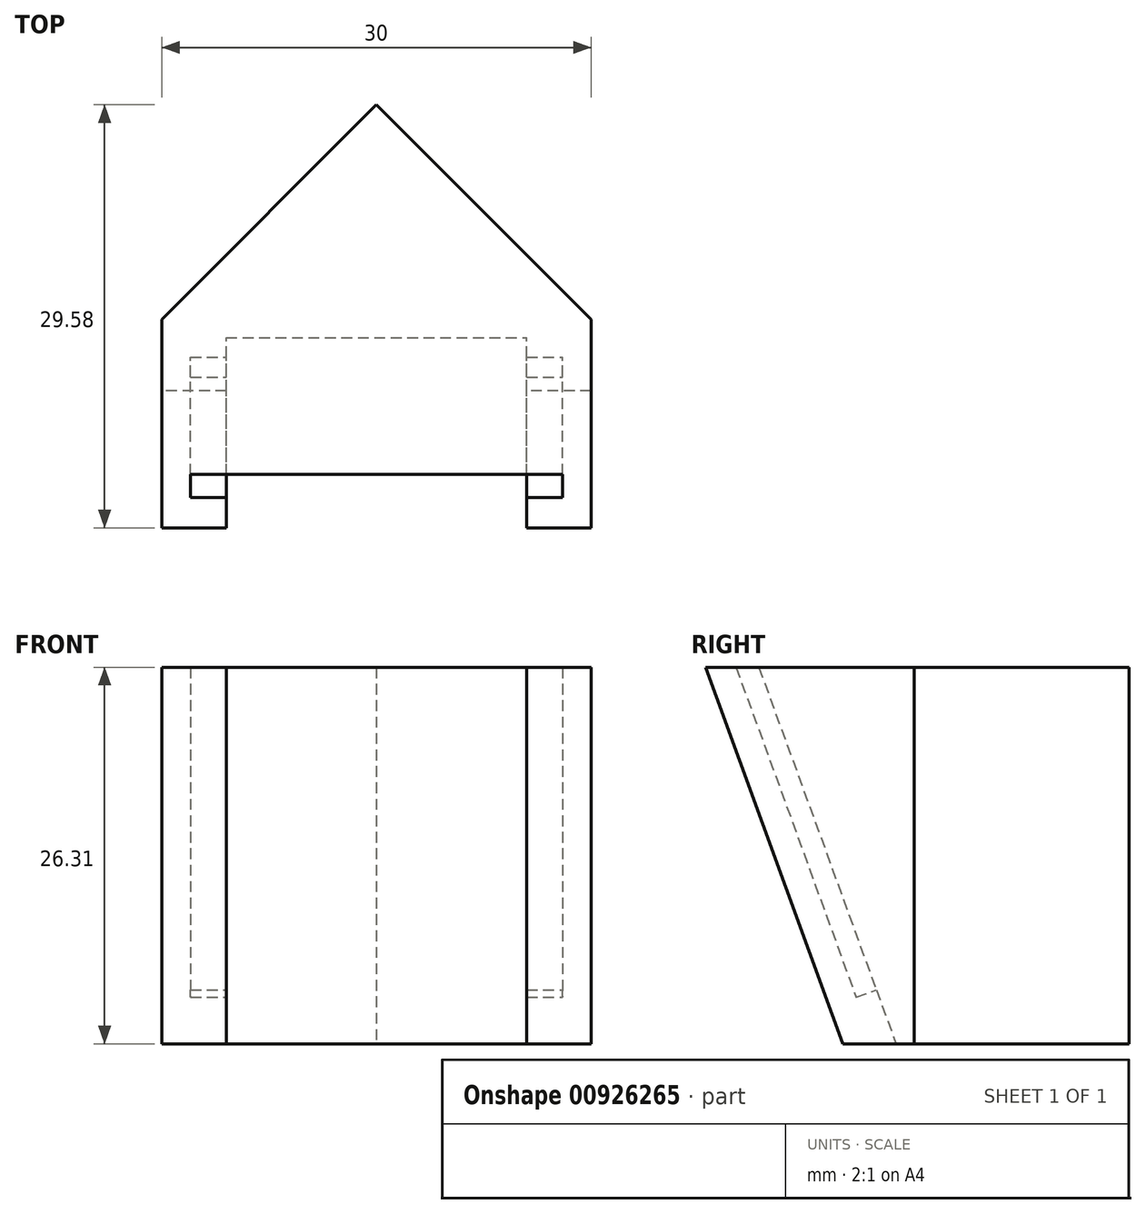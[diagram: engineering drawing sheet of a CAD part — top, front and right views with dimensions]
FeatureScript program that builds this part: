
annotation { "Feature Type Name" : "Feature", "Feature Type Description" : "" }
export const myFeature = defineFeature(function(context is Context, id is Id, definition is map)
    precondition{}
    {
        {
            var Q0;
            Q0=qCreatedBy(makeId("Right.planeOp"),FACE);
            var sketch = newSketch(context, id + "F0", { "sketchPlane" : qUnion([Q0])});
            skLineSegment(sketch, "E0", {"start": v(-15, 0) * mm, "end": v(15, 0) * mm});
            skLineSegment(sketch, "E1", {"start": v(15, 0) * mm, "end": v(15, 26.31) * mm});
            skLineSegment(sketch, "E2", {"start": v(15, 26.31) * mm, "end": v(-24.58, 26.31) * mm});
            skLineSegment(sketch, "E3", {"start": v(-24.58, 26.31) * mm, "end": v(-15, 0) * mm});
            skLineSegment(sketch, "E4", {"start": v(-19.79, 13.16) * mm, "end": v(-46.54, 21.77) * mm, "construction": true});
            skLineSegment(sketch, "E5", {"start": v(-19.79, 13.16) * mm, "end": v(-34.57, -10.36) * mm, "construction": true});
            skLineSegment(sketch, "E6", {"start": v(-20.85, 26.31) * mm, "end": v(-11.28, 0) * mm});
            skLineSegment(sketch, "E7", {"start": v(-22.45, 26.31) * mm, "end": v(-12.87, 0) * mm});
            skLineSegment(sketch, "E8", {"start": v(-14.05, 3.25) * mm, "end": v(-12.64, 3.76) * mm});
            skLineSegment(sketch, "E9", {"start": v(-20.85, 26.31) * mm, "end": v(-22.26, 25.8) * mm, "construction": true});
            skSolve(sketch);
        }
        {
            var Q0;
            {var subQ0=sQuery(id+"F0.wireOp",EDGE,"E3");Q0=makeQuery(id+"F0.imprint","IMPRINT",FACE,{"disambiguationData":[TD([[makeQuery(id+"F0.imprint","IMPRINT",EDGE,{"derivedFrom":subQ0}),1.0]])]});}
            var Q1;
            {var subQ5=sQuery(id+"F0.wireOp",EDGE,"E8");Q1=makeQuery(id+"F0.imprint","IMPRINT",FACE,{"disambiguationData":[TD([[makeQuery(id+"F0.imprint","IMPRINT",EDGE,{"derivedFrom":subQ5}),1.0]])]});}
            var Q2;
            {var subQ5=sQuery(id+"F0.wireOp",EDGE,"E8");Q2=makeQuery(id+"F0.imprint","IMPRINT",FACE,{"disambiguationData":[TD([[makeQuery(id+"F0.imprint","IMPRINT",EDGE,{"derivedFrom":subQ5}),-1.0]])]});}
            var Q3;
            {var subQ1=sQuery(id+"F0.wireOp",EDGE,"E1");Q3=makeQuery(id+"F0.imprint","IMPRINT",FACE,{"disambiguationData":[TD([[makeQuery(id+"F0.imprint","IMPRINT",EDGE,{"derivedFrom":subQ1}),1.0]])]});}
            extrude(context, id + "F1", {"entities" : qUnion([Q0, Q1, Q2, Q3]), "depth" : 30 * mm, "offsetDistance" : 25 * mm, "symmetric" : true});
        }
        {
            var Q0;
            {var subQ5=sQuery(id+"F0.wireOp",EDGE,"E8");Q0=makeQuery(id+"F0.imprint","IMPRINT",FACE,{"disambiguationData":[TD([[makeQuery(id+"F0.imprint","IMPRINT",EDGE,{"derivedFrom":subQ5}),1.0]])]});}
            extrude(context, id + "F2", {"entities" : qUnion([Q0]), "operationType" : NewBodyOperationType.REMOVE, "oppositeDirection" : true, "depth" : 26 * mm, "offsetDistance" : 25 * mm, "symmetric" : true});
        }
        {
            var Q0;
            {var subQ0=sQuery(id+"F0.wireOp",EDGE,"E3");Q0=makeQuery(id+"F0.imprint","IMPRINT",FACE,{"disambiguationData":[TD([[makeQuery(id+"F0.imprint","IMPRINT",EDGE,{"derivedFrom":subQ0}),1.0]])]});}
            extrude(context, id + "F3", {"entities" : qUnion([Q0]), "operationType" : NewBodyOperationType.REMOVE, "oppositeDirection" : true, "depth" : 21 * mm, "offsetDistance" : 25 * mm, "symmetric" : true});
        }
        {
            var Q0;
            {var subQ5=sQuery(id+"F0.wireOp",EDGE,"E8");Q0=makeQuery(id+"F0.imprint","IMPRINT",FACE,{"disambiguationData":[TD([[makeQuery(id+"F0.imprint","IMPRINT",EDGE,{"derivedFrom":subQ5}),-1.0]])]});}
            extrude(context, id + "F4", {"entities" : qUnion([Q0]), "operationType" : NewBodyOperationType.REMOVE, "oppositeDirection" : true, "depth" : 21 * mm, "offsetDistance" : 25 * mm, "symmetric" : true});
        }
        {
            var Q0;
            Q0=makeQuery(id+"F1.opExtrude","SWEPT_FACE",FACE,{"disambiguationData":[OSD([sQuery(id+"F0.wireOp",EDGE,"E0")])]});
            var sketch = newSketch(context, id + "F5", { "sketchPlane" : qUnion([Q0])});
            skLineSegment(sketch, "E10.0", {"start": v(-15, 15) * mm, "end": v(-15, -15) * mm});
            skLineSegment(sketch, "E10.1", {"start": v(15, -15) * mm, "end": v(-15, -15) * mm});
            skLineSegment(sketch, "E10.2", {"start": v(15, 15) * mm, "end": v(15, -15) * mm});
            skLineSegment(sketch, "E11.0", {"start": v(-10.5, 15) * mm, "end": v(-15, 15) * mm});
            skLineSegment(sketch, "E11.1", {"start": v(-10.5, 11.28) * mm, "end": v(10.5, 11.28) * mm});
            skLineSegment(sketch, "E11.2", {"start": v(-10.5, 15) * mm, "end": v(-10.5, 11.28) * mm});
            skLineSegment(sketch, "E11.3", {"start": v(10.5, 15) * mm, "end": v(10.5, 11.28) * mm});
            skLineSegment(sketch, "E11.4", {"start": v(15, 15) * mm, "end": v(10.5, 15) * mm});
            skLineSegment(sketch, "E12", {"start": v(0, -5) * mm, "end": v(-15, 10) * mm});
            skLineSegment(sketch, "E13", {"start": v(0, -5) * mm, "end": v(15, 10) * mm});
            skSolve(sketch);
        }
        {
            var Q0;
            {var subQ2=sQuery(id+"F5.wireOp",EDGE,"E10.1");Q0=makeQuery(id+"F5.imprint","IMPRINT",FACE,{"disambiguationData":[TD([[makeQuery(id+"F5.imprint","IMPRINT",EDGE,{"derivedFrom":subQ2}),-1.0]])]});}
            extrude(context, id + "F6", {"entities" : qUnion([Q0]), "operationType" : NewBodyOperationType.REMOVE, "oppositeDirection" : true, "depth" : 30 * mm, "offsetDistance" : 25 * mm});
        }
    });
